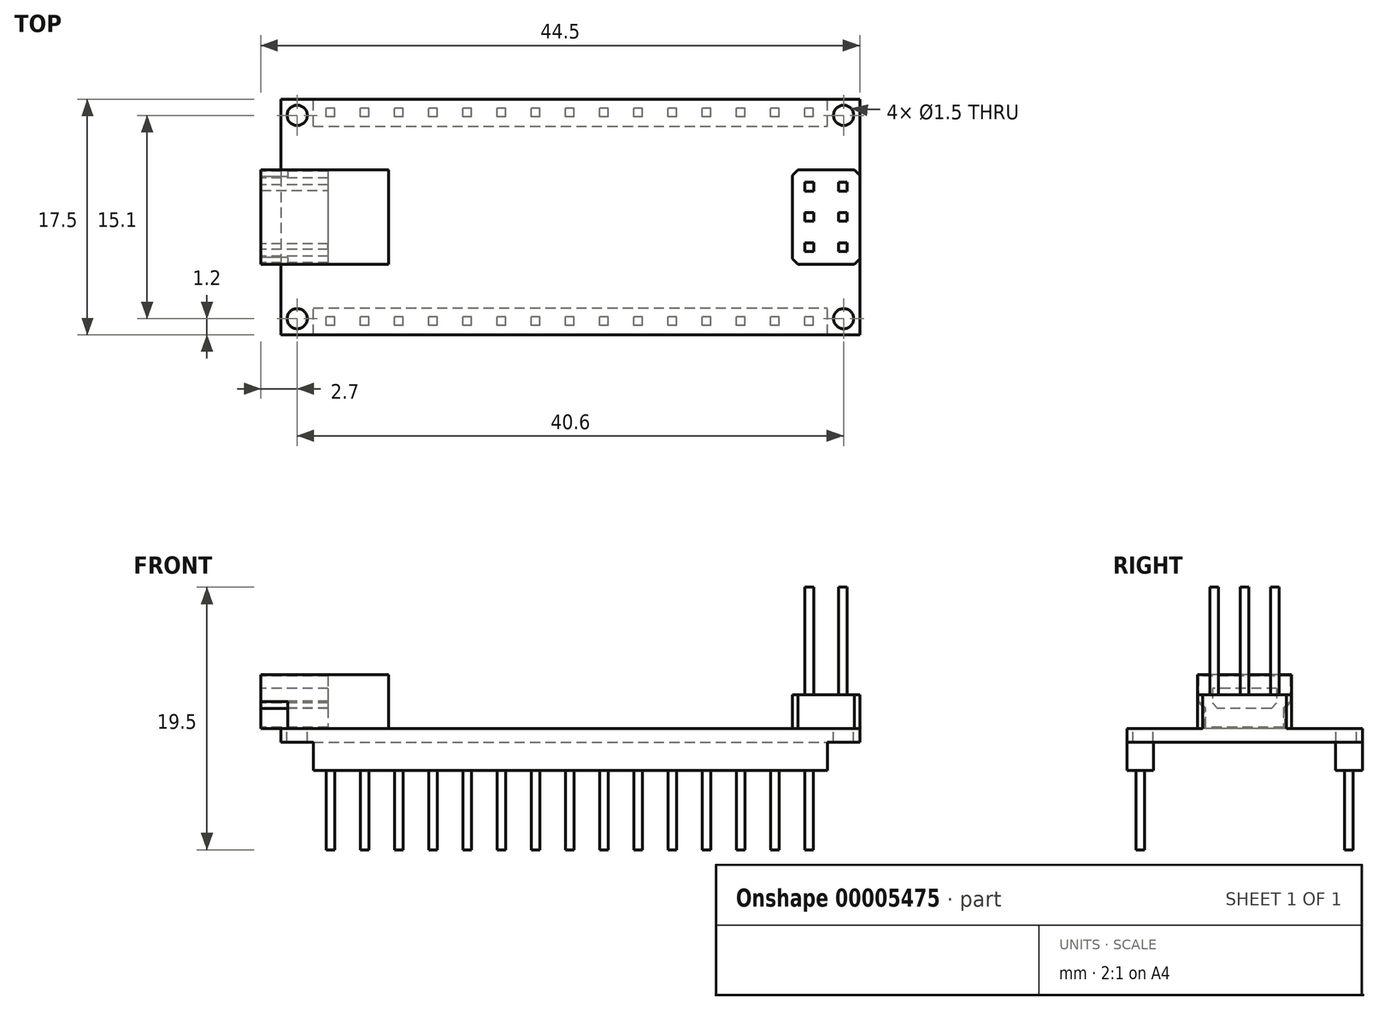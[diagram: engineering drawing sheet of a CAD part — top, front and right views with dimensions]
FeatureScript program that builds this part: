
annotation { "Feature Type Name" : "Feature", "Feature Type Description" : "" }
export const myFeature = defineFeature(function(context is Context, id is Id, definition is map)
    precondition{}
    {
        {
            var Q0;
            Q0=qCreatedBy(makeId("Top.planeOp"),FACE);
            var sketch = newSketch(context, id + "F0", { "sketchPlane" : qUnion([Q0])});
            skLineSegment(sketch, "E0.bottom", {"start": v(21.5, 8.75) * mm, "end": v(-21.5, 8.75) * mm});
            skLineSegment(sketch, "E0.top", {"start": v(21.5, -8.75) * mm, "end": v(-21.5, -8.75) * mm});
            skLineSegment(sketch, "E0.left", {"start": v(21.5, 8.75) * mm, "end": v(21.5, -8.75) * mm});
            skLineSegment(sketch, "E0.right", {"start": v(-21.5, 8.75) * mm, "end": v(-21.5, -8.75) * mm});
            skPoint(sketch, "E0.middle", {"position": v(0, 0) * mm});
            skCircle(sketch, "E1", {"center": v(-20.3, 7.55) * mm, "radius": 0.75 * mm});
            skCircle(sketch, "E2.0.1.0", {"center": v(-20.3, -7.55) * mm, "radius": 0.75 * mm});
            skCircle(sketch, "E2.1.0.0", {"center": v(20.3, 7.55) * mm, "radius": 0.75 * mm});
            skCircle(sketch, "E2.1.1.0", {"center": v(20.3, -7.55) * mm, "radius": 0.75 * mm});
            skLineSegment(sketch, "E2.direction1", {"start": v(-20.3, 7.55) * mm, "end": v(20.3, 7.55) * mm, "construction": true});
            skLineSegment(sketch, "E2.direction2", {"start": v(-20.3, 7.55) * mm, "end": v(-20.3, -7.55) * mm, "construction": true});
            skPoint(sketch, "E3", {"position": v(21.5, 0) * mm});
            skPoint(sketch, "E4", {"position": v(-21.5, 0) * mm});
            skLineSegment(sketch, "E5.bottom", {"start": v(-23, 3.5) * mm, "end": v(-13.5, 3.5) * mm});
            skLineSegment(sketch, "E5.top", {"start": v(-23, -3.5) * mm, "end": v(-13.5, -3.5) * mm});
            skLineSegment(sketch, "E5.left", {"start": v(-23, 3.5) * mm, "end": v(-23, -3.5) * mm});
            skLineSegment(sketch, "E5.right", {"start": v(-13.5, 3.5) * mm, "end": v(-13.5, -3.5) * mm});
            skPoint(sketch, "E6", {"position": v(-13.5, 0) * mm});
            skLineSegment(sketch, "E7.bottom", {"start": v(21.5, 3.5) * mm, "end": v(16.5, 3.5) * mm});
            skLineSegment(sketch, "E7.top", {"start": v(21.5, -3.5) * mm, "end": v(16.5, -3.5) * mm});
            skLineSegment(sketch, "E7.left", {"start": v(21.5, 3.5) * mm, "end": v(21.5, -3.5) * mm});
            skLineSegment(sketch, "E7.right", {"start": v(16.5, 3.5) * mm, "end": v(16.5, -3.5) * mm});
            skSolve(sketch);
        }
        {
            var Q0;
            {var subQ5=sQuery(id+"F0.wireOp",EDGE,"E5.right");Q0=makeQuery(id+"F0.imprint","IMPRINT",FACE,{"disambiguationData":[TD([[makeQuery(id+"F0.imprint","IMPRINT",EDGE,{"derivedFrom":subQ5}),-1.0]])]});}
            var Q1;
            {var subQ0=sQuery(id+"F0.wireOp",EDGE,"E0.bottom");Q1=makeQuery(id+"F0.imprint","IMPRINT",FACE,{"disambiguationData":[TD([[makeQuery(id+"F0.imprint","IMPRINT",EDGE,{"derivedFrom":subQ0}),1.0]])]});}
            var Q2;
            Q2=makeQuery(id+"F0.imprint","IMPRINT",FACE,{"disambiguationData":[TD([[makeQuery(id+"F0.imprint","IMPRINT",EDGE,{"derivedFrom":sQuery(id+"F0.wireOp",EDGE,"E7.bottom")}),1.0]])]});
            extrude(context, id + "F1", {"entities" : qUnion([Q0, Q1, Q2]), "oppositeDirection" : true, "depth" : 1 * mm});
        }
        {
            var Q0;
            {var subQ5=sQuery(id+"F0.wireOp",EDGE,"E5.left");Q0=makeQuery(id+"F0.imprint","IMPRINT",FACE,{"disambiguationData":[TD([[makeQuery(id+"F0.imprint","IMPRINT",EDGE,{"derivedFrom":subQ5}),1.0]])]});}
            var Q1;
            {var subQ5=sQuery(id+"F0.wireOp",EDGE,"E5.right");Q1=makeQuery(id+"F0.imprint","IMPRINT",FACE,{"disambiguationData":[TD([[makeQuery(id+"F0.imprint","IMPRINT",EDGE,{"derivedFrom":subQ5}),-1.0]])]});}
            extrude(context, id + "F2", {"entities" : qUnion([Q0, Q1]), "operationType" : NewBodyOperationType.ADD, "depth" : 4 * mm});
        }
        {
            var Q0;
            Q0=makeQuery(id+"F0.imprint","IMPRINT",FACE,{"disambiguationData":[TD([[makeQuery(id+"F0.imprint","IMPRINT",EDGE,{"derivedFrom":sQuery(id+"F0.wireOp",EDGE,"E7.bottom")}),1.0]])]});
            extrude(context, id + "F3", {"entities" : qUnion([Q0]), "operationType" : NewBodyOperationType.ADD, "depth" : 2.5 * mm});
        }
        {
            var Q0;
            Q0=makeQuery(id+"F2.opExtrude","SWEPT_FACE",FACE,{"disambiguationData":[OSD([sQuery(id+"F0.wireOp",EDGE,"E5.left")])]});
            var sketch = newSketch(context, id + "F4", { "sketchPlane" : qUnion([Q0])});
            skPoint(sketch, "E8", {"position": v(-3.5, 2) * mm});
            skPoint(sketch, "E9", {"position": v(3.5, 2) * mm});
            skPoint(sketch, "E10", {"position": v(-3, 0) * mm});
            skPoint(sketch, "E11", {"position": v(3, 0) * mm});
            skPoint(sketch, "E12", {"position": v(-3, 1.5) * mm});
            skPoint(sketch, "E13", {"position": v(3, 1.5) * mm});
            skLineSegment(sketch, "E14", {"start": v(-3.5, 2) * mm, "end": v(-3, 1.5) * mm});
            skLineSegment(sketch, "E15", {"start": v(-3, 0) * mm, "end": v(-3, 1.5) * mm});
            skLineSegment(sketch, "E16", {"start": v(3, 0) * mm, "end": v(3, 1.5) * mm});
            skLineSegment(sketch, "E17", {"start": v(3, 1.5) * mm, "end": v(3.5, 2) * mm});
            skLineSegment(sketch, "E18.bottom", {"start": v(-2.4, 3) * mm, "end": v(2.4, 3) * mm});
            skLineSegment(sketch, "E18.top", {"start": v(-2.4, 1.5) * mm, "end": v(2.4, 1.5) * mm});
            skLineSegment(sketch, "E18.left", {"start": v(-2.4, 3) * mm, "end": v(-2.4, 1.5) * mm});
            skLineSegment(sketch, "E18.right", {"start": v(2.4, 3) * mm, "end": v(2.4, 1.5) * mm});
            skPoint(sketch, "E19", {"position": v(0, 3) * mm});
            skPoint(sketch, "E20", {"position": v(-2.4, 2.25) * mm});
            skPoint(sketch, "E21", {"position": v(-3.5, 4) * mm});
            skPoint(sketch, "E22", {"position": v(3.5, 4) * mm});
            skLineSegment(sketch, "E23.0", {"start": v(-3.5, -1) * mm, "end": v(3.5, -1) * mm});
            skLineSegment(sketch, "E24", {"start": v(-3.5, 4) * mm, "end": v(-3.5, 2) * mm});
            skLineSegment(sketch, "E25", {"start": v(-3, 1.5) * mm, "end": v(-3, 0) * mm});
            skLineSegment(sketch, "E26", {"start": v(-3, 0) * mm, "end": v(3, 0) * mm});
            skLineSegment(sketch, "E27", {"start": v(3.5, 2) * mm, "end": v(3.5, 4) * mm});
            skLineSegment(sketch, "E28.0", {"start": v(-3.4, 3.9) * mm, "end": v(3.4, 3.9) * mm});
            skLineSegment(sketch, "E28.1", {"start": v(3.4, 2.04) * mm, "end": v(3.4, 3.9) * mm});
            skLineSegment(sketch, "E28.2", {"start": v(-3.4, 3.9) * mm, "end": v(-3.4, 2.04) * mm});
            skLineSegment(sketch, "E28.3", {"start": v(2.9, 1.54) * mm, "end": v(3.4, 2.04) * mm});
            skLineSegment(sketch, "E28.4", {"start": v(-3.4, 2.04) * mm, "end": v(-2.9, 1.54) * mm});
            skLineSegment(sketch, "E28.5", {"start": v(-2.9, 1.54) * mm, "end": v(-2.9, 0.1) * mm});
            skLineSegment(sketch, "E28.6", {"start": v(-2.9, 0.1) * mm, "end": v(2.9, 0.1) * mm});
            skLineSegment(sketch, "E28.7", {"start": v(2.9, 0.1) * mm, "end": v(2.9, 1.54) * mm});
            skPoint(sketch, "E29", {"position": v(-3.4, 2.04) * mm});
            skPoint(sketch, "E30", {"position": v(-2.9, 1.54) * mm});
            skSolve(sketch);
        }
        {
            var Q0;
            Q0=makeQuery(id+"F4.imprint","IMPRINT",FACE,{"disambiguationData":[TD([[makeQuery(id+"F4.imprint","IMPRINT",EDGE,{"derivedFrom":sQuery(id+"F4.wireOp",EDGE,"E18.bottom")}),1.0]])]});
            extrude(context, id + "F5", {"entities" : qUnion([Q0]), "operationType" : NewBodyOperationType.REMOVE, "oppositeDirection" : true, "depth" : 5 * mm});
        }
        {
            var Q0;
            {var subQ0=sQuery(id+"F4.wireOp",EDGE,"E14");Q0=makeQuery(id+"F4.imprint","IMPRINT",FACE,{"disambiguationData":[TD([[makeQuery(id+"F4.imprint","IMPRINT",EDGE,{"derivedFrom":subQ0}),-1.0]])]});}
            var Q1;
            {var subQ0=sQuery(id+"F4.wireOp",EDGE,"E16");Q1=makeQuery(id+"F4.imprint","IMPRINT",FACE,{"disambiguationData":[TD([[makeQuery(id+"F4.imprint","IMPRINT",EDGE,{"derivedFrom":subQ0}),-1.0]])]});}
            extrude(context, id + "F6", {"entities" : qUnion([Q0, Q1]), "operationType" : NewBodyOperationType.REMOVE, "oppositeDirection" : true, "depth" : 2 * mm});
        }
        {
            var Q0;
            Q0=makeQuery(id+"F1.opExtrude","CAP_FACE",FACE,{"disambiguationData":[OSD([sQuery(id+"F0.wireOp",EDGE,"E0.bottom"),sQuery(id+"F0.wireOp",EDGE,"E0.top"),sQuery(id+"F0.wireOp",EDGE,"E0.left"),sQuery(id+"F0.wireOp",EDGE,"E0.right"),sQuery(id+"F0.wireOp",EDGE,"E1"),sQuery(id+"F0.wireOp",EDGE,"E2.0.1.0"),sQuery(id+"F0.wireOp",EDGE,"E2.1.0.0"),sQuery(id+"F0.wireOp",EDGE,"E2.1.1.0"),sQuery(id+"F0.wireOp",EDGE,"E7.left")])],"isStart":false});
            var sketch = newSketch(context, id + "F7", { "sketchPlane" : qUnion([Q0])});
            skLineSegment(sketch, "E31.bottom", {"start": v(-19.1, 8.75) * mm, "end": v(19.1, 8.75) * mm});
            skLineSegment(sketch, "E31.top", {"start": v(-19.1, 6.75) * mm, "end": v(19.1, 6.75) * mm});
            skLineSegment(sketch, "E31.left", {"start": v(-19.1, 8.75) * mm, "end": v(-19.1, 6.75) * mm});
            skLineSegment(sketch, "E31.right", {"start": v(19.1, 8.75) * mm, "end": v(19.1, 6.75) * mm});
            skPoint(sketch, "E32", {"position": v(0, 6.75) * mm});
            skLineSegment(sketch, "E33", {"start": v(-19.1, 7.75) * mm, "end": v(19.1, 7.75) * mm, "construction": true});
            skPoint(sketch, "E34", {"position": v(-17.83, 7.75) * mm});
            skLineSegment(sketch, "E35.bottom", {"start": v(-17.51, 8.07) * mm, "end": v(-18.15, 8.07) * mm});
            skLineSegment(sketch, "E35.top", {"start": v(-17.51, 7.43) * mm, "end": v(-18.15, 7.43) * mm});
            skLineSegment(sketch, "E35.left", {"start": v(-17.51, 8.07) * mm, "end": v(-17.51, 7.43) * mm});
            skLineSegment(sketch, "E35.right", {"start": v(-18.15, 8.07) * mm, "end": v(-18.15, 7.43) * mm});
            skPoint(sketch, "E36.1.0.0", {"position": v(-15.3, 7.75) * mm});
            skLineSegment(sketch, "E36.1.0.1", {"start": v(-14.97, 8.07) * mm, "end": v(-14.97, 7.43) * mm});
            skLineSegment(sketch, "E36.1.0.2", {"start": v(-14.97, 8.07) * mm, "end": v(-15.61, 8.07) * mm});
            skLineSegment(sketch, "E36.1.0.3", {"start": v(-15.61, 8.07) * mm, "end": v(-15.61, 7.43) * mm});
            skLineSegment(sketch, "E36.1.0.4", {"start": v(-14.97, 7.43) * mm, "end": v(-15.61, 7.43) * mm});
            skPoint(sketch, "E36.2.0.0", {"position": v(-12.75, 7.75) * mm});
            skLineSegment(sketch, "E36.2.0.1", {"start": v(-12.43, 8.07) * mm, "end": v(-12.43, 7.43) * mm});
            skLineSegment(sketch, "E36.2.0.2", {"start": v(-12.43, 8.07) * mm, "end": v(-13.07, 8.07) * mm});
            skLineSegment(sketch, "E36.2.0.3", {"start": v(-13.07, 8.07) * mm, "end": v(-13.07, 7.43) * mm});
            skLineSegment(sketch, "E36.2.0.4", {"start": v(-12.43, 7.43) * mm, "end": v(-13.07, 7.43) * mm});
            skPoint(sketch, "E36.3.0.0", {"position": v(-10.21, 7.75) * mm});
            skLineSegment(sketch, "E36.3.0.1", {"start": v(-9.89, 8.07) * mm, "end": v(-9.89, 7.43) * mm});
            skLineSegment(sketch, "E36.3.0.2", {"start": v(-9.89, 8.07) * mm, "end": v(-10.53, 8.07) * mm});
            skLineSegment(sketch, "E36.3.0.3", {"start": v(-10.53, 8.07) * mm, "end": v(-10.53, 7.43) * mm});
            skLineSegment(sketch, "E36.3.0.4", {"start": v(-9.89, 7.43) * mm, "end": v(-10.53, 7.43) * mm});
            skPoint(sketch, "E36.4.0.0", {"position": v(-7.67, 7.75) * mm});
            skLineSegment(sketch, "E36.4.0.1", {"start": v(-7.35, 8.07) * mm, "end": v(-7.35, 7.43) * mm});
            skLineSegment(sketch, "E36.4.0.2", {"start": v(-7.35, 8.07) * mm, "end": v(-8, 8.07) * mm});
            skLineSegment(sketch, "E36.4.0.3", {"start": v(-8, 8.07) * mm, "end": v(-8, 7.43) * mm});
            skLineSegment(sketch, "E36.4.0.4", {"start": v(-7.35, 7.43) * mm, "end": v(-8, 7.43) * mm});
            skPoint(sketch, "E36.5.0.0", {"position": v(-5.13, 7.75) * mm});
            skLineSegment(sketch, "E36.5.0.1", {"start": v(-4.8, 8.07) * mm, "end": v(-4.8, 7.43) * mm});
            skLineSegment(sketch, "E36.5.0.2", {"start": v(-4.8, 8.07) * mm, "end": v(-5.45, 8.07) * mm});
            skLineSegment(sketch, "E36.5.0.3", {"start": v(-5.45, 8.07) * mm, "end": v(-5.45, 7.43) * mm});
            skLineSegment(sketch, "E36.5.0.4", {"start": v(-4.8, 7.43) * mm, "end": v(-5.45, 7.43) * mm});
            skPoint(sketch, "E36.6.0.0", {"position": v(-2.59, 7.75) * mm});
            skLineSegment(sketch, "E36.6.0.1", {"start": v(-2.27, 8.07) * mm, "end": v(-2.27, 7.43) * mm});
            skLineSegment(sketch, "E36.6.0.2", {"start": v(-2.27, 8.07) * mm, "end": v(-2.9, 8.07) * mm});
            skLineSegment(sketch, "E36.6.0.3", {"start": v(-2.9, 8.07) * mm, "end": v(-2.9, 7.43) * mm});
            skLineSegment(sketch, "E36.6.0.4", {"start": v(-2.27, 7.43) * mm, "end": v(-2.9, 7.43) * mm});
            skPoint(sketch, "E36.7.0.0", {"position": v(-0.05, 7.75) * mm});
            skLineSegment(sketch, "E36.7.0.1", {"start": v(0.27, 8.07) * mm, "end": v(0.27, 7.43) * mm});
            skLineSegment(sketch, "E36.7.0.2", {"start": v(0.27, 8.07) * mm, "end": v(-0.37, 8.07) * mm});
            skLineSegment(sketch, "E36.7.0.3", {"start": v(-0.37, 8.07) * mm, "end": v(-0.37, 7.43) * mm});
            skLineSegment(sketch, "E36.7.0.4", {"start": v(0.27, 7.43) * mm, "end": v(-0.37, 7.43) * mm});
            skPoint(sketch, "E36.8.0.0", {"position": v(2.5, 7.75) * mm});
            skLineSegment(sketch, "E36.8.0.1", {"start": v(2.81, 8.07) * mm, "end": v(2.81, 7.43) * mm});
            skLineSegment(sketch, "E36.8.0.2", {"start": v(2.81, 8.07) * mm, "end": v(2.17, 8.07) * mm});
            skLineSegment(sketch, "E36.8.0.3", {"start": v(2.17, 8.07) * mm, "end": v(2.17, 7.43) * mm});
            skLineSegment(sketch, "E36.8.0.4", {"start": v(2.81, 7.43) * mm, "end": v(2.17, 7.43) * mm});
            skPoint(sketch, "E36.9.0.0", {"position": v(5.03, 7.75) * mm});
            skLineSegment(sketch, "E36.9.0.1", {"start": v(5.35, 8.07) * mm, "end": v(5.35, 7.43) * mm});
            skLineSegment(sketch, "E36.9.0.2", {"start": v(5.35, 8.07) * mm, "end": v(4.71, 8.07) * mm});
            skLineSegment(sketch, "E36.9.0.3", {"start": v(4.71, 8.07) * mm, "end": v(4.71, 7.43) * mm});
            skLineSegment(sketch, "E36.9.0.4", {"start": v(5.35, 7.43) * mm, "end": v(4.71, 7.43) * mm});
            skPoint(sketch, "E36.10.0.0", {"position": v(7.57, 7.75) * mm});
            skLineSegment(sketch, "E36.10.0.1", {"start": v(7.9, 8.07) * mm, "end": v(7.9, 7.43) * mm});
            skLineSegment(sketch, "E36.10.0.2", {"start": v(7.9, 8.07) * mm, "end": v(7.25, 8.07) * mm});
            skLineSegment(sketch, "E36.10.0.3", {"start": v(7.25, 8.07) * mm, "end": v(7.25, 7.43) * mm});
            skLineSegment(sketch, "E36.10.0.4", {"start": v(7.9, 7.43) * mm, "end": v(7.25, 7.43) * mm});
            skPoint(sketch, "E36.11.0.0", {"position": v(10.11, 7.75) * mm});
            skLineSegment(sketch, "E36.11.0.1", {"start": v(10.43, 8.07) * mm, "end": v(10.43, 7.43) * mm});
            skLineSegment(sketch, "E36.11.0.2", {"start": v(10.43, 8.07) * mm, "end": v(9.8, 8.07) * mm});
            skLineSegment(sketch, "E36.11.0.3", {"start": v(9.8, 8.07) * mm, "end": v(9.8, 7.43) * mm});
            skLineSegment(sketch, "E36.11.0.4", {"start": v(10.43, 7.43) * mm, "end": v(9.8, 7.43) * mm});
            skPoint(sketch, "E36.12.0.0", {"position": v(12.65, 7.75) * mm});
            skLineSegment(sketch, "E36.12.0.1", {"start": v(12.97, 8.07) * mm, "end": v(12.97, 7.43) * mm});
            skLineSegment(sketch, "E36.12.0.2", {"start": v(12.97, 8.07) * mm, "end": v(12.33, 8.07) * mm});
            skLineSegment(sketch, "E36.12.0.3", {"start": v(12.33, 8.07) * mm, "end": v(12.33, 7.43) * mm});
            skLineSegment(sketch, "E36.12.0.4", {"start": v(12.97, 7.43) * mm, "end": v(12.33, 7.43) * mm});
            skPoint(sketch, "E36.13.0.0", {"position": v(15.2, 7.75) * mm});
            skLineSegment(sketch, "E36.13.0.1", {"start": v(15.51, 8.07) * mm, "end": v(15.51, 7.43) * mm});
            skLineSegment(sketch, "E36.13.0.2", {"start": v(15.51, 8.07) * mm, "end": v(14.87, 8.07) * mm});
            skLineSegment(sketch, "E36.13.0.3", {"start": v(14.87, 8.07) * mm, "end": v(14.87, 7.43) * mm});
            skLineSegment(sketch, "E36.13.0.4", {"start": v(15.51, 7.43) * mm, "end": v(14.87, 7.43) * mm});
            skPoint(sketch, "E36.14.0.0", {"position": v(17.73, 7.75) * mm});
            skLineSegment(sketch, "E36.14.0.1", {"start": v(18.05, 8.07) * mm, "end": v(18.05, 7.43) * mm});
            skLineSegment(sketch, "E36.14.0.2", {"start": v(18.05, 8.07) * mm, "end": v(17.41, 8.07) * mm});
            skLineSegment(sketch, "E36.14.0.3", {"start": v(17.41, 8.07) * mm, "end": v(17.41, 7.43) * mm});
            skLineSegment(sketch, "E36.14.0.4", {"start": v(18.05, 7.43) * mm, "end": v(17.41, 7.43) * mm});
            skLineSegment(sketch, "E36.direction1", {"start": v(-17.83, 7.75) * mm, "end": v(-15.3, 7.75) * mm, "construction": true});
            skPoint(sketch, "E37", {"position": v(-20.3, 7.55) * mm});
            skLineSegment(sketch, "E38", {"start": v(-20.3, 7.55) * mm, "end": v(-21.5, 7.55) * mm});
            skLineSegment(sketch, "E39", {"start": v(-21.5, 7.55) * mm, "end": v(-19.1, 7.55) * mm});
            skPoint(sketch, "E40", {"position": v(-21.05, 7.55) * mm});
            skPoint(sketch, "E41", {"position": v(-19.55, 7.55) * mm});
            skPoint(sketch, "E42", {"position": v(20.3, 7.55) * mm});
            skLineSegment(sketch, "E43", {"start": v(20.3, 7.55) * mm, "end": v(21.5, 7.55) * mm});
            skLineSegment(sketch, "E44", {"start": v(21.5, 7.55) * mm, "end": v(19.1, 7.55) * mm});
            skPoint(sketch, "E45", {"position": v(21.05, 7.55) * mm});
            skPoint(sketch, "E46", {"position": v(19.55, 7.55) * mm});
            skPoint(sketch, "E47.0.1.0", {"position": v(-0.05, -7.75) * mm});
            skPoint(sketch, "E47.0.1.1", {"position": v(-5.13, -7.75) * mm});
            skPoint(sketch, "E47.0.1.2", {"position": v(12.65, -7.75) * mm});
            skPoint(sketch, "E47.0.1.3", {"position": v(-7.67, -7.75) * mm});
            skPoint(sketch, "E47.0.1.4", {"position": v(17.73, -7.75) * mm});
            skPoint(sketch, "E47.0.1.5", {"position": v(-10.21, -7.75) * mm});
            skPoint(sketch, "E47.0.1.6", {"position": v(7.57, -7.75) * mm});
            skPoint(sketch, "E47.0.1.7", {"position": v(2.49, -7.75) * mm});
            skPoint(sketch, "E47.0.1.8", {"position": v(0, -8.75) * mm});
            skPoint(sketch, "E47.0.1.9", {"position": v(-17.83, -7.75) * mm});
            skPoint(sketch, "E47.0.1.10", {"position": v(5.03, -7.75) * mm});
            skPoint(sketch, "E47.0.1.11", {"position": v(-15.3, -7.75) * mm});
            skLineSegment(sketch, "E47.0.1.12", {"start": v(-17.83, -7.75) * mm, "end": v(-15.3, -7.75) * mm, "construction": true});
            skPoint(sketch, "E47.0.1.13", {"position": v(10.11, -7.75) * mm});
            skPoint(sketch, "E47.0.1.14", {"position": v(15.2, -7.75) * mm});
            skPoint(sketch, "E47.0.1.15", {"position": v(-2.6, -7.75) * mm});
            skPoint(sketch, "E47.0.1.16", {"position": v(-12.75, -7.75) * mm});
            skPoint(sketch, "E47.0.1.17", {"position": v(-17.83, -7.75) * mm});
            skLineSegment(sketch, "E47.0.1.18", {"start": v(18.05, -7.43) * mm, "end": v(17.41, -7.43) * mm});
            skLineSegment(sketch, "E47.0.1.19", {"start": v(18.05, -8.07) * mm, "end": v(17.41, -8.07) * mm});
            skLineSegment(sketch, "E47.0.1.20", {"start": v(18.05, -7.43) * mm, "end": v(18.05, -8.07) * mm});
            skLineSegment(sketch, "E47.0.1.21", {"start": v(-0.37, -7.43) * mm, "end": v(-0.37, -8.07) * mm});
            skLineSegment(sketch, "E47.0.1.22", {"start": v(-10.53, -7.43) * mm, "end": v(-10.53, -8.07) * mm});
            skLineSegment(sketch, "E47.0.1.23", {"start": v(-9.89, -7.43) * mm, "end": v(-10.53, -7.43) * mm});
            skLineSegment(sketch, "E47.0.1.24", {"start": v(-2.27, -7.43) * mm, "end": v(-2.9, -7.43) * mm});
            skLineSegment(sketch, "E47.0.1.25", {"start": v(12.97, -7.43) * mm, "end": v(12.97, -8.07) * mm});
            skLineSegment(sketch, "E47.0.1.26", {"start": v(-5.45, -7.43) * mm, "end": v(-5.45, -8.07) * mm});
            skLineSegment(sketch, "E47.0.1.27", {"start": v(-7.35, -8.07) * mm, "end": v(-7.99, -8.07) * mm});
            skLineSegment(sketch, "E47.0.1.28", {"start": v(2.81, -8.07) * mm, "end": v(2.17, -8.07) * mm});
            skLineSegment(sketch, "E47.0.1.29", {"start": v(12.97, -8.07) * mm, "end": v(12.33, -8.07) * mm});
            skLineSegment(sketch, "E47.0.1.30", {"start": v(7.9, -8.07) * mm, "end": v(7.25, -8.07) * mm});
            skLineSegment(sketch, "E47.0.1.31", {"start": v(7.25, -7.43) * mm, "end": v(7.25, -8.07) * mm});
            skLineSegment(sketch, "E47.0.1.32", {"start": v(-2.9, -7.43) * mm, "end": v(-2.9, -8.07) * mm});
            skLineSegment(sketch, "E47.0.1.33", {"start": v(-7.35, -7.43) * mm, "end": v(-7.99, -7.43) * mm});
            skLineSegment(sketch, "E47.0.1.34", {"start": v(2.81, -7.43) * mm, "end": v(2.81, -8.07) * mm});
            skLineSegment(sketch, "E47.0.1.35", {"start": v(7.9, -7.43) * mm, "end": v(7.25, -7.43) * mm});
            skLineSegment(sketch, "E47.0.1.36", {"start": v(-4.8, -8.07) * mm, "end": v(-5.45, -8.07) * mm});
            skLineSegment(sketch, "E47.0.1.37", {"start": v(-7.35, -7.43) * mm, "end": v(-7.35, -8.07) * mm});
            skLineSegment(sketch, "E47.0.1.38", {"start": v(15.5, -8.07) * mm, "end": v(14.87, -8.07) * mm});
            skLineSegment(sketch, "E47.0.1.39", {"start": v(5.35, -8.07) * mm, "end": v(4.71, -8.07) * mm});
            skLineSegment(sketch, "E47.0.1.40", {"start": v(-2.27, -8.07) * mm, "end": v(-2.9, -8.07) * mm});
            skLineSegment(sketch, "E47.0.1.41", {"start": v(-12.43, -8.07) * mm, "end": v(-13.07, -8.07) * mm});
            skLineSegment(sketch, "E47.0.1.42", {"start": v(2.81, -7.43) * mm, "end": v(2.17, -7.43) * mm});
            skLineSegment(sketch, "E47.0.1.43", {"start": v(17.41, -7.43) * mm, "end": v(17.41, -8.07) * mm});
            skLineSegment(sketch, "E47.0.1.44", {"start": v(12.97, -7.43) * mm, "end": v(12.33, -7.43) * mm});
            skLineSegment(sketch, "E47.0.1.45", {"start": v(7.9, -7.43) * mm, "end": v(7.9, -8.07) * mm});
            skLineSegment(sketch, "E47.0.1.46", {"start": v(-2.27, -7.43) * mm, "end": v(-2.27, -8.07) * mm});
            skLineSegment(sketch, "E47.0.1.47", {"start": v(-17.5, -8.07) * mm, "end": v(-18.15, -8.07) * mm});
            skLineSegment(sketch, "E47.0.1.48", {"start": v(12.33, -7.43) * mm, "end": v(12.33, -8.07) * mm});
            skLineSegment(sketch, "E47.0.1.49", {"start": v(-14.97, -7.43) * mm, "end": v(-14.97, -8.07) * mm});
            skLineSegment(sketch, "E47.0.1.50", {"start": v(2.17, -7.43) * mm, "end": v(2.17, -8.07) * mm});
            skLineSegment(sketch, "E47.0.1.51", {"start": v(-8, -7.43) * mm, "end": v(-8, -8.07) * mm});
            skLineSegment(sketch, "E47.0.1.52", {"start": v(-14.97, -7.43) * mm, "end": v(-15.6, -7.43) * mm});
            skLineSegment(sketch, "E47.0.1.53", {"start": v(-15.61, -7.43) * mm, "end": v(-15.61, -8.07) * mm});
            skLineSegment(sketch, "E47.0.1.54", {"start": v(-14.97, -8.07) * mm, "end": v(-15.6, -8.07) * mm});
            skLineSegment(sketch, "E47.0.1.55", {"start": v(-9.89, -7.43) * mm, "end": v(-9.89, -8.07) * mm});
            skLineSegment(sketch, "E47.0.1.56", {"start": v(0.27, -7.43) * mm, "end": v(0.27, -8.07) * mm});
            skLineSegment(sketch, "E47.0.1.57", {"start": v(10.43, -7.43) * mm, "end": v(10.43, -8.07) * mm});
            skLineSegment(sketch, "E47.0.1.58", {"start": v(-12.43, -7.43) * mm, "end": v(-12.43, -8.07) * mm});
            skLineSegment(sketch, "E47.0.1.59", {"start": v(10.43, -7.43) * mm, "end": v(9.8, -7.43) * mm});
            skLineSegment(sketch, "E47.0.1.60", {"start": v(0.27, -7.43) * mm, "end": v(-0.37, -7.43) * mm});
            skLineSegment(sketch, "E47.0.1.61", {"start": v(15.51, -7.43) * mm, "end": v(15.51, -8.07) * mm});
            skLineSegment(sketch, "E47.0.1.62", {"start": v(5.35, -7.43) * mm, "end": v(5.35, -8.07) * mm});
            skLineSegment(sketch, "E47.0.1.63", {"start": v(-4.8, -7.43) * mm, "end": v(-4.8, -8.07) * mm});
            skLineSegment(sketch, "E47.0.1.64", {"start": v(15.51, -7.43) * mm, "end": v(14.87, -7.43) * mm});
            skLineSegment(sketch, "E47.0.1.65", {"start": v(5.35, -7.43) * mm, "end": v(4.71, -7.43) * mm});
            skLineSegment(sketch, "E47.0.1.66", {"start": v(-4.8, -7.43) * mm, "end": v(-5.45, -7.43) * mm});
            skLineSegment(sketch, "E47.0.1.67", {"start": v(10.43, -8.07) * mm, "end": v(9.8, -8.07) * mm});
            skLineSegment(sketch, "E47.0.1.68", {"start": v(0.27, -8.07) * mm, "end": v(-0.37, -8.07) * mm});
            skLineSegment(sketch, "E47.0.1.69", {"start": v(-9.9, -8.07) * mm, "end": v(-10.53, -8.07) * mm});
            skLineSegment(sketch, "E47.0.1.70", {"start": v(4.71, -7.43) * mm, "end": v(4.71, -8.07) * mm});
            skLineSegment(sketch, "E47.0.1.71", {"start": v(14.87, -7.43) * mm, "end": v(14.87, -8.07) * mm});
            skLineSegment(sketch, "E47.0.1.72", {"start": v(9.8, -7.43) * mm, "end": v(9.8, -8.07) * mm});
            skLineSegment(sketch, "E47.0.1.73", {"start": v(-12.43, -7.43) * mm, "end": v(-13.07, -7.43) * mm});
            skLineSegment(sketch, "E47.0.1.74", {"start": v(-13.07, -7.43) * mm, "end": v(-13.07, -8.07) * mm});
            skLineSegment(sketch, "E47.0.1.75", {"start": v(-18.15, -7.43) * mm, "end": v(-18.15, -8.07) * mm});
            skLineSegment(sketch, "E47.0.1.76", {"start": v(-17.51, -7.43) * mm, "end": v(-17.51, -8.07) * mm});
            skLineSegment(sketch, "E47.0.1.77", {"start": v(-17.5, -7.43) * mm, "end": v(-18.15, -7.43) * mm});
            skLineSegment(sketch, "E47.0.1.78", {"start": v(19.1, -6.75) * mm, "end": v(19.1, -8.75) * mm});
            skLineSegment(sketch, "E47.0.1.79", {"start": v(-19.1, -8.75) * mm, "end": v(19.1, -8.75) * mm});
            skLineSegment(sketch, "E47.0.1.80", {"start": v(-19.1, -6.75) * mm, "end": v(-19.1, -8.75) * mm});
            skLineSegment(sketch, "E47.0.1.81", {"start": v(-19.1, -6.75) * mm, "end": v(19.1, -6.75) * mm});
            skLineSegment(sketch, "E47.direction1", {"start": v(-0.05, 7.75) * mm, "end": v(24.95, 7.75) * mm, "construction": true});
            skLineSegment(sketch, "E47.direction2", {"start": v(-0.05, 7.75) * mm, "end": v(-0.05, -7.75) * mm, "construction": true});
            skSolve(sketch);
        }
        {
            var Q0;
            Q0=makeQuery(id+"F7.imprint","IMPRINT",FACE,{"disambiguationData":[TD([[makeQuery(id+"F7.imprint","IMPRINT",EDGE,{"derivedFrom":sQuery(id+"F7.wireOp",EDGE,"E47.0.1.18")}),-1.0]])]});
            var Q1;
            {var subQ1=sQuery(id+"F7.wireOp",EDGE,"E31.bottom");Q1=makeQuery(id+"F7.imprint","IMPRINT",FACE,{"disambiguationData":[TD([[makeQuery(id+"F7.imprint","IMPRINT",EDGE,{"derivedFrom":subQ1}),1.0]])]});}
            extrude(context, id + "F8", {"entities" : qUnion([Q0, Q1]), "depth" : 2.1 * mm});
        }
        {
            var Q0;
            Q0=makeQuery(id+"F7.imprint","IMPRINT",FACE,{"disambiguationData":[TD([[makeQuery(id+"F7.imprint","IMPRINT",EDGE,{"derivedFrom":sQuery(id+"F7.wireOp",EDGE,"E35.bottom")}),1.0]])]});
            var Q1;
            Q1=makeQuery(id+"F7.imprint","IMPRINT",FACE,{"disambiguationData":[TD([[makeQuery(id+"F7.imprint","IMPRINT",EDGE,{"derivedFrom":sQuery(id+"F7.wireOp",EDGE,"E36.1.0.1")}),-1.0]])]});
            var Q2;
            Q2=makeQuery(id+"F7.imprint","IMPRINT",FACE,{"disambiguationData":[TD([[makeQuery(id+"F7.imprint","IMPRINT",EDGE,{"derivedFrom":sQuery(id+"F7.wireOp",EDGE,"E36.2.0.1")}),-1.0]])]});
            var Q3;
            Q3=makeQuery(id+"F7.imprint","IMPRINT",FACE,{"disambiguationData":[TD([[makeQuery(id+"F7.imprint","IMPRINT",EDGE,{"derivedFrom":sQuery(id+"F7.wireOp",EDGE,"E36.3.0.1")}),-1.0]])]});
            var Q4;
            Q4=makeQuery(id+"F7.imprint","IMPRINT",FACE,{"disambiguationData":[TD([[makeQuery(id+"F7.imprint","IMPRINT",EDGE,{"derivedFrom":sQuery(id+"F7.wireOp",EDGE,"E36.4.0.1")}),-1.0]])]});
            var Q5;
            Q5=makeQuery(id+"F7.imprint","IMPRINT",FACE,{"disambiguationData":[TD([[makeQuery(id+"F7.imprint","IMPRINT",EDGE,{"derivedFrom":sQuery(id+"F7.wireOp",EDGE,"E36.5.0.1")}),-1.0]])]});
            var Q6;
            Q6=makeQuery(id+"F7.imprint","IMPRINT",FACE,{"disambiguationData":[TD([[makeQuery(id+"F7.imprint","IMPRINT",EDGE,{"derivedFrom":sQuery(id+"F7.wireOp",EDGE,"E36.6.0.1")}),-1.0]])]});
            var Q7;
            Q7=makeQuery(id+"F7.imprint","IMPRINT",FACE,{"disambiguationData":[TD([[makeQuery(id+"F7.imprint","IMPRINT",EDGE,{"derivedFrom":sQuery(id+"F7.wireOp",EDGE,"E36.7.0.1")}),-1.0]])]});
            var Q8;
            Q8=makeQuery(id+"F7.imprint","IMPRINT",FACE,{"disambiguationData":[TD([[makeQuery(id+"F7.imprint","IMPRINT",EDGE,{"derivedFrom":sQuery(id+"F7.wireOp",EDGE,"E36.8.0.1")}),-1.0]])]});
            var Q9;
            Q9=makeQuery(id+"F7.imprint","IMPRINT",FACE,{"disambiguationData":[TD([[makeQuery(id+"F7.imprint","IMPRINT",EDGE,{"derivedFrom":sQuery(id+"F7.wireOp",EDGE,"E36.9.0.1")}),-1.0]])]});
            var Q10;
            Q10=makeQuery(id+"F7.imprint","IMPRINT",FACE,{"disambiguationData":[TD([[makeQuery(id+"F7.imprint","IMPRINT",EDGE,{"derivedFrom":sQuery(id+"F7.wireOp",EDGE,"E36.10.0.1")}),-1.0]])]});
            var Q11;
            Q11=makeQuery(id+"F7.imprint","IMPRINT",FACE,{"disambiguationData":[TD([[makeQuery(id+"F7.imprint","IMPRINT",EDGE,{"derivedFrom":sQuery(id+"F7.wireOp",EDGE,"E36.11.0.1")}),-1.0]])]});
            var Q12;
            Q12=makeQuery(id+"F7.imprint","IMPRINT",FACE,{"disambiguationData":[TD([[makeQuery(id+"F7.imprint","IMPRINT",EDGE,{"derivedFrom":sQuery(id+"F7.wireOp",EDGE,"E36.12.0.1")}),-1.0]])]});
            var Q13;
            Q13=makeQuery(id+"F7.imprint","IMPRINT",FACE,{"disambiguationData":[TD([[makeQuery(id+"F7.imprint","IMPRINT",EDGE,{"derivedFrom":sQuery(id+"F7.wireOp",EDGE,"E36.13.0.1")}),-1.0]])]});
            var Q14;
            Q14=makeQuery(id+"F7.imprint","IMPRINT",FACE,{"disambiguationData":[TD([[makeQuery(id+"F7.imprint","IMPRINT",EDGE,{"derivedFrom":sQuery(id+"F7.wireOp",EDGE,"E36.14.0.1")}),-1.0]])]});
            var Q15;
            Q15=makeQuery(id+"F7.imprint","IMPRINT",FACE,{"disambiguationData":[TD([[makeQuery(id+"F7.imprint","IMPRINT",EDGE,{"derivedFrom":sQuery(id+"F7.wireOp",EDGE,"E47.0.1.47")}),-1.0]])]});
            var Q16;
            Q16=makeQuery(id+"F7.imprint","IMPRINT",FACE,{"disambiguationData":[TD([[makeQuery(id+"F7.imprint","IMPRINT",EDGE,{"derivedFrom":sQuery(id+"F7.wireOp",EDGE,"E47.0.1.49")}),-1.0]])]});
            var Q17;
            Q17=makeQuery(id+"F7.imprint","IMPRINT",FACE,{"disambiguationData":[TD([[makeQuery(id+"F7.imprint","IMPRINT",EDGE,{"derivedFrom":sQuery(id+"F7.wireOp",EDGE,"E47.0.1.41")}),-1.0]])]});
            var Q18;
            Q18=makeQuery(id+"F7.imprint","IMPRINT",FACE,{"disambiguationData":[TD([[makeQuery(id+"F7.imprint","IMPRINT",EDGE,{"derivedFrom":sQuery(id+"F7.wireOp",EDGE,"E47.0.1.22")}),1.0]])]});
            var Q19;
            Q19=makeQuery(id+"F7.imprint","IMPRINT",FACE,{"disambiguationData":[TD([[makeQuery(id+"F7.imprint","IMPRINT",EDGE,{"derivedFrom":sQuery(id+"F7.wireOp",EDGE,"E47.0.1.27")}),-1.0]])]});
            var Q20;
            Q20=makeQuery(id+"F7.imprint","IMPRINT",FACE,{"disambiguationData":[TD([[makeQuery(id+"F7.imprint","IMPRINT",EDGE,{"derivedFrom":sQuery(id+"F7.wireOp",EDGE,"E47.0.1.26")}),1.0]])]});
            var Q21;
            Q21=makeQuery(id+"F7.imprint","IMPRINT",FACE,{"disambiguationData":[TD([[makeQuery(id+"F7.imprint","IMPRINT",EDGE,{"derivedFrom":sQuery(id+"F7.wireOp",EDGE,"E47.0.1.24")}),1.0]])]});
            var Q22;
            Q22=makeQuery(id+"F7.imprint","IMPRINT",FACE,{"disambiguationData":[TD([[makeQuery(id+"F7.imprint","IMPRINT",EDGE,{"derivedFrom":sQuery(id+"F7.wireOp",EDGE,"E47.0.1.21")}),1.0]])]});
            var Q23;
            Q23=makeQuery(id+"F7.imprint","IMPRINT",FACE,{"disambiguationData":[TD([[makeQuery(id+"F7.imprint","IMPRINT",EDGE,{"derivedFrom":sQuery(id+"F7.wireOp",EDGE,"E47.0.1.28")}),-1.0]])]});
            var Q24;
            Q24=makeQuery(id+"F7.imprint","IMPRINT",FACE,{"disambiguationData":[TD([[makeQuery(id+"F7.imprint","IMPRINT",EDGE,{"derivedFrom":sQuery(id+"F7.wireOp",EDGE,"E47.0.1.39")}),-1.0]])]});
            var Q25;
            Q25=makeQuery(id+"F7.imprint","IMPRINT",FACE,{"disambiguationData":[TD([[makeQuery(id+"F7.imprint","IMPRINT",EDGE,{"derivedFrom":sQuery(id+"F7.wireOp",EDGE,"E47.0.1.30")}),-1.0]])]});
            var Q26;
            Q26=makeQuery(id+"F7.imprint","IMPRINT",FACE,{"disambiguationData":[TD([[makeQuery(id+"F7.imprint","IMPRINT",EDGE,{"derivedFrom":sQuery(id+"F7.wireOp",EDGE,"E47.0.1.57")}),-1.0]])]});
            var Q27;
            Q27=makeQuery(id+"F7.imprint","IMPRINT",FACE,{"disambiguationData":[TD([[makeQuery(id+"F7.imprint","IMPRINT",EDGE,{"derivedFrom":sQuery(id+"F7.wireOp",EDGE,"E47.0.1.25")}),-1.0]])]});
            var Q28;
            Q28=makeQuery(id+"F7.imprint","IMPRINT",FACE,{"disambiguationData":[TD([[makeQuery(id+"F7.imprint","IMPRINT",EDGE,{"derivedFrom":sQuery(id+"F7.wireOp",EDGE,"E47.0.1.38")}),-1.0]])]});
            var Q29;
            Q29=makeQuery(id+"F7.imprint","IMPRINT",FACE,{"disambiguationData":[TD([[makeQuery(id+"F7.imprint","IMPRINT",EDGE,{"derivedFrom":sQuery(id+"F7.wireOp",EDGE,"E47.0.1.18")}),1.0]])]});
            extrude(context, id + "F9", {"entities" : qUnion([Q0, Q1, Q2, Q3, Q4, Q5, Q6, Q7, Q8, Q9, Q10, Q11, Q12, Q13, Q14, Q15, Q16, Q17, Q18, Q19, Q20, Q21, Q22, Q23, Q24, Q25, Q26, Q27, Q28, Q29]), "operationType" : NewBodyOperationType.ADD, "depth" : 8 * mm});
        }
        {
            var Q0;
            Q0=makeQuery(id+"F5.boolean.opBoolean","COPY",EDGE,{"derivedFrom":makeQuery(id+"F5.opExtrude","SWEPT_EDGE",EDGE,{"disambiguationData":[OSD([sQuery(id+"F4.wireOp",EDGE,"E18.top"),sQuery(id+"F4.wireOp",EDGE,"E18.right")])]})});
            var Q1;
            Q1=makeQuery(id+"F5.boolean.opBoolean","COPY",EDGE,{"derivedFrom":makeQuery(id+"F5.opExtrude","SWEPT_EDGE",EDGE,{"disambiguationData":[OSD([sQuery(id+"F4.wireOp",EDGE,"E18.top"),sQuery(id+"F4.wireOp",EDGE,"E18.left")])]})});
            chamfer(context, id + "F10", {"entities" : qUnion([Q0, Q1]), "width" : 0.4 * mm, "tangentPropagation" : true});
        }
        {
            var Q0;
            Q0=makeQuery(id+"F3.opExtrude","CAP_FACE",FACE,{"disambiguationData":[OSD([sQuery(id+"F0.wireOp",EDGE,"E7.bottom"),sQuery(id+"F0.wireOp",EDGE,"E7.top"),sQuery(id+"F0.wireOp",EDGE,"E7.left"),sQuery(id+"F0.wireOp",EDGE,"E7.right")])],"isStart":false});
            var sketch = newSketch(context, id + "F11", { "sketchPlane" : qUnion([Q0])});
            skPoint(sketch, "E48", {"position": v(21.5, 1.17) * mm});
            skPoint(sketch, "E49", {"position": v(21.5, -1.17) * mm});
            skLineSegment(sketch, "E50", {"start": v(21.5, 3.5) * mm, "end": v(21.5, 1.17) * mm});
            skLineSegment(sketch, "E51", {"start": v(21.5, -1.17) * mm, "end": v(21.5, 1.17) * mm});
            skLineSegment(sketch, "E52", {"start": v(21.5, -1.17) * mm, "end": v(21.5, -3.5) * mm});
            skLineSegment(sketch, "E53", {"start": v(21.5, 1.17) * mm, "end": v(16.5, 1.17) * mm});
            skLineSegment(sketch, "E54", {"start": v(21.5, -1.17) * mm, "end": v(16.5, -1.17) * mm});
            skPoint(sketch, "E55", {"position": v(19, 3.5) * mm});
            skPoint(sketch, "E56", {"position": v(19, -3.5) * mm});
            skLineSegment(sketch, "E57", {"start": v(19, 3.5) * mm, "end": v(19, -3.5) * mm});
            skPoint(sketch, "E58", {"position": v(17.75, 2.25) * mm});
            skLineSegment(sketch, "E59", {"start": v(17.75, 2.25) * mm, "end": v(17.75, 3.5) * mm, "construction": true});
            skLineSegment(sketch, "E60", {"start": v(17.75, 2.25) * mm, "end": v(16.5, 2.25) * mm, "construction": true});
            skLineSegment(sketch, "E61", {"start": v(17.75, 2.25) * mm, "end": v(19, 2.25) * mm, "construction": true});
            skLineSegment(sketch, "E62", {"start": v(17.75, 2.25) * mm, "end": v(17.75, 1.17) * mm, "construction": true});
            skLineSegment(sketch, "E63.bottom", {"start": v(18.07, 2.57) * mm, "end": v(17.43, 2.57) * mm});
            skLineSegment(sketch, "E63.top", {"start": v(18.07, 1.93) * mm, "end": v(17.43, 1.93) * mm});
            skLineSegment(sketch, "E63.left", {"start": v(18.07, 2.57) * mm, "end": v(18.07, 1.93) * mm});
            skLineSegment(sketch, "E63.right", {"start": v(17.43, 2.57) * mm, "end": v(17.43, 1.93) * mm});
            skLineSegment(sketch, "E64.1.0.0", {"start": v(20.57, 2.57) * mm, "end": v(20.57, 1.93) * mm});
            skLineSegment(sketch, "E64.1.0.1", {"start": v(20.57, 2.57) * mm, "end": v(19.93, 2.57) * mm});
            skLineSegment(sketch, "E64.1.0.2", {"start": v(19.93, 2.57) * mm, "end": v(19.93, 1.93) * mm});
            skLineSegment(sketch, "E64.1.0.3", {"start": v(20.57, 1.93) * mm, "end": v(19.93, 1.93) * mm});
            skPoint(sketch, "E65", {"position": v(20.25, 2.25) * mm});
            skLineSegment(sketch, "E66", {"start": v(19, 2.25) * mm, "end": v(20.25, 2.25) * mm, "construction": true});
            skLineSegment(sketch, "E67", {"start": v(20.25, 2.25) * mm, "end": v(21.5, 2.25) * mm, "construction": true});
            skLineSegment(sketch, "E68", {"start": v(20.25, 3.5) * mm, "end": v(20.25, 2.25) * mm, "construction": true});
            skPoint(sketch, "E68.startSnap0", {"position": v(20.25, 2.57) * mm});
            skLineSegment(sketch, "E69", {"start": v(20.25, 1.17) * mm, "end": v(20.25, 2.25) * mm, "construction": true});
            skPoint(sketch, "E70", {"position": v(21.5, 0) * mm});
            skPoint(sketch, "E71.0.1.0", {"position": v(20.25, 0) * mm});
            skLineSegment(sketch, "E71.0.1.1", {"start": v(20.57, 0.32) * mm, "end": v(20.57, -0.32) * mm});
            skLineSegment(sketch, "E71.0.1.2", {"start": v(20.57, 0.32) * mm, "end": v(19.93, 0.32) * mm});
            skLineSegment(sketch, "E71.0.1.3", {"start": v(19.93, 0.32) * mm, "end": v(19.93, -0.32) * mm});
            skLineSegment(sketch, "E71.0.1.4", {"start": v(20.57, -0.32) * mm, "end": v(19.93, -0.32) * mm});
            skLineSegment(sketch, "E71.0.1.5", {"start": v(18.07, 0.32) * mm, "end": v(18.07, -0.32) * mm});
            skLineSegment(sketch, "E71.0.1.6", {"start": v(18.07, -0.32) * mm, "end": v(17.43, -0.32) * mm});
            skLineSegment(sketch, "E71.0.1.7", {"start": v(17.43, 0.32) * mm, "end": v(17.43, -0.32) * mm});
            skLineSegment(sketch, "E71.0.1.8", {"start": v(18.07, 0.32) * mm, "end": v(17.43, 0.32) * mm});
            skPoint(sketch, "E71.0.2.0", {"position": v(20.25, -2.25) * mm});
            skLineSegment(sketch, "E71.0.2.1", {"start": v(20.57, -1.93) * mm, "end": v(20.57, -2.57) * mm});
            skLineSegment(sketch, "E71.0.2.2", {"start": v(20.57, -1.93) * mm, "end": v(19.93, -1.93) * mm});
            skLineSegment(sketch, "E71.0.2.3", {"start": v(19.93, -1.93) * mm, "end": v(19.93, -2.57) * mm});
            skLineSegment(sketch, "E71.0.2.4", {"start": v(20.57, -2.57) * mm, "end": v(19.93, -2.57) * mm});
            skLineSegment(sketch, "E71.0.2.5", {"start": v(18.07, -1.93) * mm, "end": v(18.07, -2.57) * mm});
            skLineSegment(sketch, "E71.0.2.6", {"start": v(18.07, -2.57) * mm, "end": v(17.43, -2.57) * mm});
            skLineSegment(sketch, "E71.0.2.7", {"start": v(17.43, -1.93) * mm, "end": v(17.43, -2.57) * mm});
            skLineSegment(sketch, "E71.0.2.8", {"start": v(18.07, -1.93) * mm, "end": v(17.43, -1.93) * mm});
            skLineSegment(sketch, "E71.direction1", {"start": v(20.25, 2.25) * mm, "end": v(31.55, 2.25) * mm, "construction": true});
            skLineSegment(sketch, "E71.direction2", {"start": v(20.25, 2.25) * mm, "end": v(20.25, 0) * mm, "construction": true});
            skSolve(sketch);
        }
        {
            var Q0;
            Q0=makeQuery(id+"F11.imprint","IMPRINT",FACE,{"disambiguationData":[TD([[makeQuery(id+"F11.imprint","IMPRINT",EDGE,{"derivedFrom":sQuery(id+"F11.wireOp",EDGE,"E71.0.2.1")}),-1.0]])]});
            var Q1;
            Q1=makeQuery(id+"F11.imprint","IMPRINT",FACE,{"disambiguationData":[TD([[makeQuery(id+"F11.imprint","IMPRINT",EDGE,{"derivedFrom":sQuery(id+"F11.wireOp",EDGE,"E71.0.2.5")}),-1.0]])]});
            var Q2;
            Q2=makeQuery(id+"F11.imprint","IMPRINT",FACE,{"disambiguationData":[TD([[makeQuery(id+"F11.imprint","IMPRINT",EDGE,{"derivedFrom":sQuery(id+"F11.wireOp",EDGE,"E71.0.1.5")}),-1.0]])]});
            var Q3;
            Q3=makeQuery(id+"F11.imprint","IMPRINT",FACE,{"disambiguationData":[TD([[makeQuery(id+"F11.imprint","IMPRINT",EDGE,{"derivedFrom":sQuery(id+"F11.wireOp",EDGE,"E71.0.1.1")}),-1.0]])]});
            var Q4;
            Q4=makeQuery(id+"F11.imprint","IMPRINT",FACE,{"disambiguationData":[TD([[makeQuery(id+"F11.imprint","IMPRINT",EDGE,{"derivedFrom":sQuery(id+"F11.wireOp",EDGE,"E64.1.0.0")}),-1.0]])]});
            var Q5;
            Q5=makeQuery(id+"F11.imprint","IMPRINT",FACE,{"disambiguationData":[TD([[makeQuery(id+"F11.imprint","IMPRINT",EDGE,{"derivedFrom":sQuery(id+"F11.wireOp",EDGE,"E63.bottom")}),1.0]])]});
            extrude(context, id + "F12", {"entities" : qUnion([Q0, Q1, Q2, Q3, Q4, Q5]), "operationType" : NewBodyOperationType.ADD, "depth" : 8 * mm});
        }
        {
            var Q0;
            Q0=makeQuery(id+"F3.opExtrude","SWEPT_EDGE",EDGE,{"disambiguationData":[OSD([sQuery(id+"F0.wireOp",EDGE,"E0.left"),sQuery(id+"F0.wireOp",EDGE,"E7.bottom"),sQuery(id+"F0.wireOp",EDGE,"E7.left")])]});
            var Q1;
            Q1=makeQuery(id+"F3.opExtrude","SWEPT_EDGE",EDGE,{"disambiguationData":[OSD([sQuery(id+"F0.wireOp",EDGE,"E7.bottom"),sQuery(id+"F0.wireOp",EDGE,"E7.right")])]});
            var Q2;
            Q2=makeQuery(id+"F3.opExtrude","SWEPT_EDGE",EDGE,{"disambiguationData":[OSD([sQuery(id+"F0.wireOp",EDGE,"E0.left"),sQuery(id+"F0.wireOp",EDGE,"E7.top"),sQuery(id+"F0.wireOp",EDGE,"E7.left")])]});
            var Q3;
            Q3=makeQuery(id+"F3.opExtrude","SWEPT_EDGE",EDGE,{"disambiguationData":[OSD([sQuery(id+"F0.wireOp",EDGE,"E7.top"),sQuery(id+"F0.wireOp",EDGE,"E7.right")])]});
            chamfer(context, id + "F13", {"entities" : qUnion([Q0, Q1, Q2, Q3]), "width" : 0.4 * mm, "tangentPropagation" : true});
        }
    });
